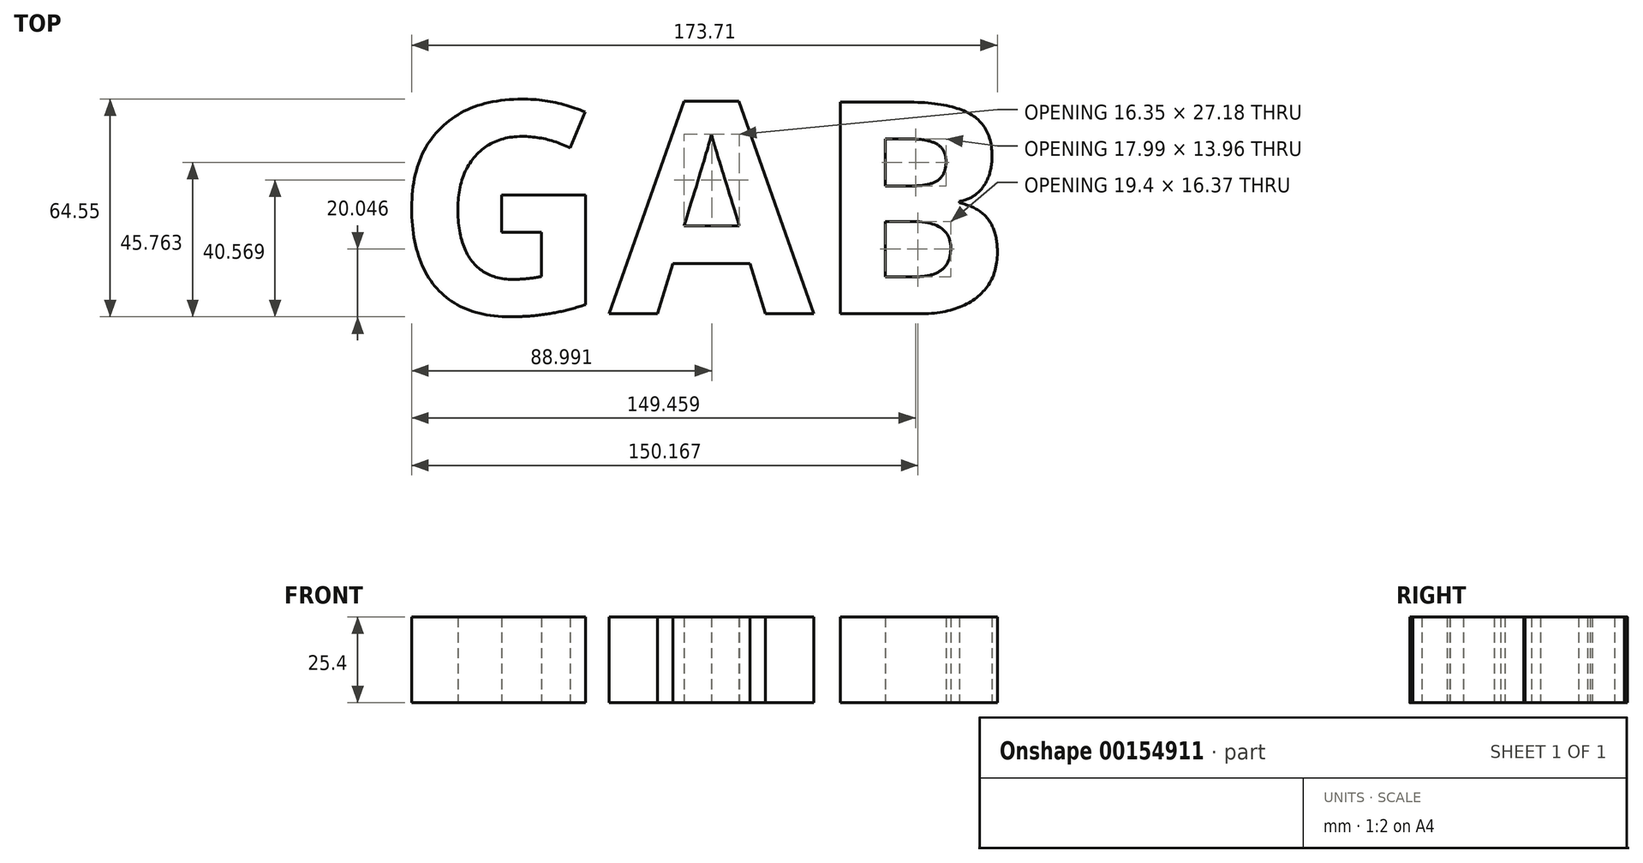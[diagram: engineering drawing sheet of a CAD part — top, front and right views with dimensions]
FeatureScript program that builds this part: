
annotation { "Feature Type Name" : "Feature", "Feature Type Description" : "" }
export const myFeature = defineFeature(function(context is Context, id is Id, definition is map)
    precondition{}
    {
        {
            var Q0;
            Q0=qCreatedBy(makeId("Top.planeOp"),FACE);
            var sketch = newSketch(context, id + "F0", { "sketchPlane" : qUnion([Q0])});
            skText(sketch, "E0", { "text": "GAB", "fontName": "OpenSans-Bold.ttf"});
            const initialGuessF0  = {"E0": [-0.11973, -0.06332, 1, 0, 0.06332]};
            skSetInitialGuess(sketch, initialGuessF0);
            skSolve(sketch);
        }
        {
            var Q0;
            Q0 = qSketchRegion(id + "F0", true);
            extrude(context, id + "F1", {"entities" : qUnion([Q0]), "depth" : 25.4 * mm});
        }
    });
